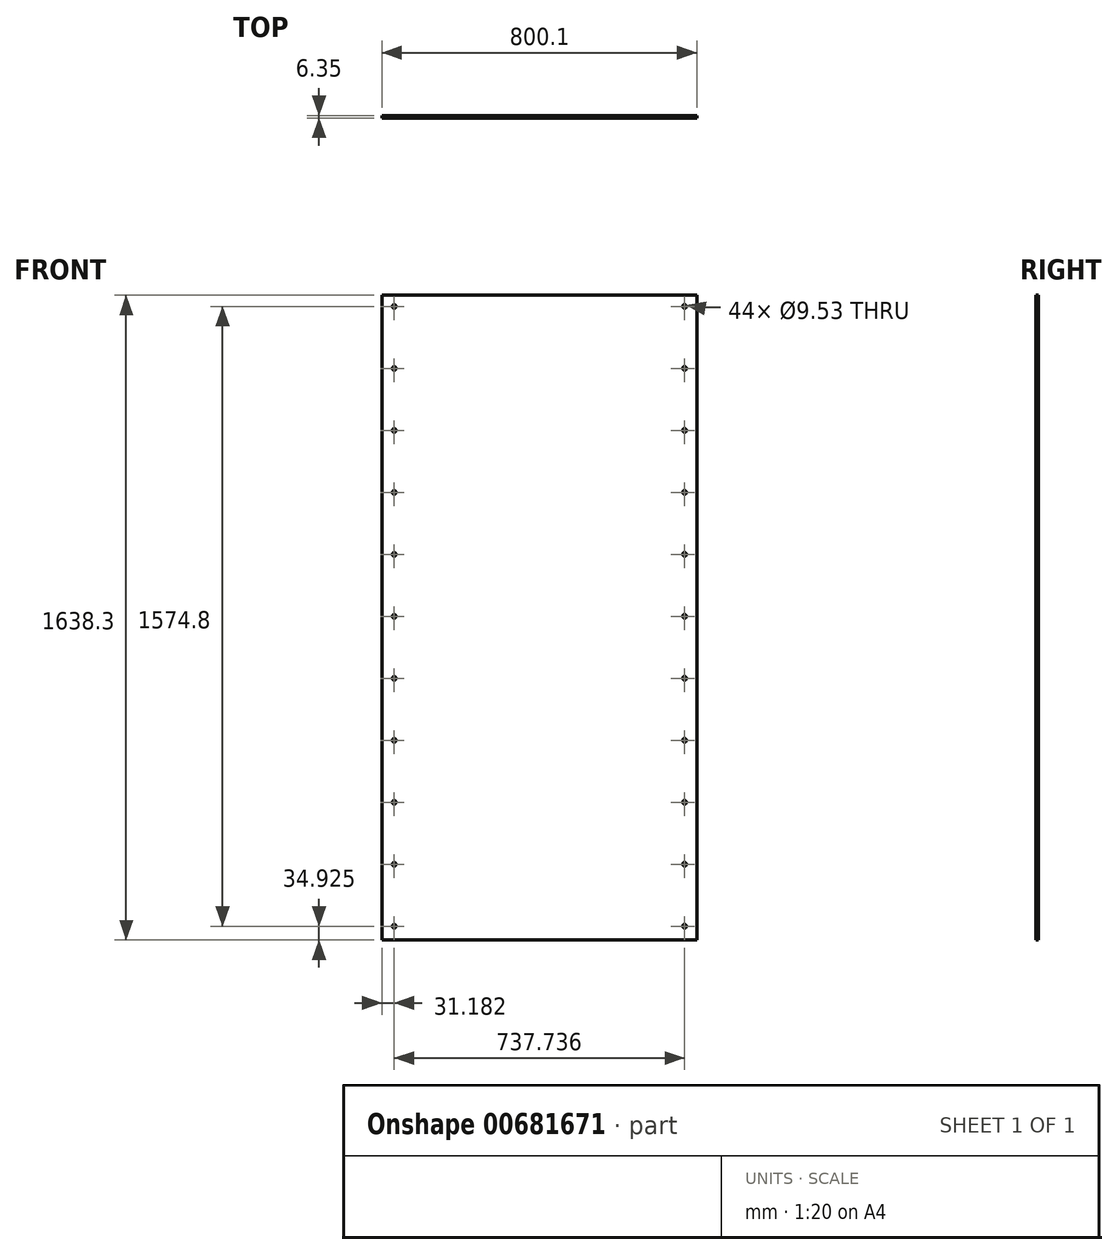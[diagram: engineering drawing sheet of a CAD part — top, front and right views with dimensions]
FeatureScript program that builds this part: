
annotation { "Feature Type Name" : "Feature", "Feature Type Description" : "" }
export const myFeature = defineFeature(function(context is Context, id is Id, definition is map)
    precondition{}
    {
        {
            var Q0;
            Q0=qCreatedBy(makeId("Front.planeOp"),FACE);
            var sketch = newSketch(context, id + "F0", { "sketchPlane" : qUnion([Q0])});
            skLineSegment(sketch, "E0.bottom", {"start": v(-400.05, 819.15) * mm, "end": v(400.05, 819.15) * mm});
            skLineSegment(sketch, "E0.top", {"start": v(-400.05, -819.15) * mm, "end": v(400.05, -819.15) * mm});
            skLineSegment(sketch, "E0.left", {"start": v(-400.05, 819.15) * mm, "end": v(-400.05, -819.15) * mm});
            skLineSegment(sketch, "E0.right", {"start": v(400.05, 819.15) * mm, "end": v(400.05, -819.15) * mm});
            skPoint(sketch, "E0.middle", {"position": v(0, 0) * mm});
            skLineSegment(sketch, "E1", {"start": v(-368.87, 819.15) * mm, "end": v(-368.87, -819.15) * mm, "construction": true});
            skLineSegment(sketch, "E2.bottom", {"start": v(-336.55, 762) * mm, "end": v(336.55, 762) * mm, "construction": true});
            skLineSegment(sketch, "E2.top", {"start": v(-336.55, -762) * mm, "end": v(336.55, -762) * mm, "construction": true});
            skLineSegment(sketch, "E2.left", {"start": v(-336.55, 762) * mm, "end": v(-336.55, -762) * mm, "construction": true});
            skLineSegment(sketch, "E2.right", {"start": v(336.55, 762) * mm, "end": v(336.55, -762) * mm, "construction": true});
            skLineSegment(sketch, "E3", {"start": v(0, 0) * mm, "end": v(-400.05, 0) * mm, "construction": true});
            skLineSegment(sketch, "E4", {"start": v(0, 0) * mm, "end": v(400.05, 0) * mm, "construction": true});
            skLineSegment(sketch, "E5", {"start": v(-431.98, 790.58) * mm, "end": v(468.8, 790.58) * mm, "construction": true});
            skLineSegment(sketch, "E6.MirrorCS", {"start": v(368.87, 819.15) * mm, "end": v(368.87, -819.15) * mm, "construction": true});
            skLineSegment(sketch, "E7.MirrorCS", {"start": v(-431.98, -790.58) * mm, "end": v(468.8, -790.57) * mm, "construction": true});
            skCircle(sketch, "E8", {"center": v(-368.87, 790.58) * mm, "radius": 4.76 * mm});
            skCircle(sketch, "E9.0.1.0", {"center": v(-368.87, 633.1) * mm, "radius": 4.76 * mm});
            skCircle(sketch, "E9.0.2.0", {"center": v(-368.87, 475.62) * mm, "radius": 4.76 * mm});
            skCircle(sketch, "E9.0.3.0", {"center": v(-368.87, 318.14) * mm, "radius": 4.76 * mm});
            skCircle(sketch, "E9.0.4.0", {"center": v(-368.87, 160.66) * mm, "radius": 4.76 * mm});
            skCircle(sketch, "E9.0.5.0", {"center": v(-368.87, 3.18) * mm, "radius": 4.76 * mm});
            skCircle(sketch, "E9.0.6.0", {"center": v(-368.87, -154.3) * mm, "radius": 4.76 * mm});
            skCircle(sketch, "E9.0.7.0", {"center": v(-368.87, -311.78) * mm, "radius": 4.76 * mm});
            skCircle(sketch, "E9.0.8.0", {"center": v(-368.87, -469.26) * mm, "radius": 4.76 * mm});
            skCircle(sketch, "E9.0.9.0", {"center": v(-368.87, -626.74) * mm, "radius": 4.76 * mm});
            skCircle(sketch, "E9.0.10.0", {"center": v(-368.87, -784.22) * mm, "radius": 4.76 * mm});
            skLineSegment(sketch, "E9.direction1", {"start": v(-368.87, 790.58) * mm, "end": v(-368.87, 790.58) * mm});
            skLineSegment(sketch, "E9.direction2", {"start": v(-368.87, 790.58) * mm, "end": v(-368.87, 633.1) * mm, "construction": true});
            skCircle(sketch, "E10.MirrorC", {"center": v(368.87, -784.22) * mm, "radius": 4.76 * mm});
            skCircle(sketch, "E11.MirrorC", {"center": v(368.87, -626.74) * mm, "radius": 4.76 * mm});
            skCircle(sketch, "E12.MirrorC", {"center": v(368.87, -469.26) * mm, "radius": 4.76 * mm});
            skCircle(sketch, "E13.MirrorC", {"center": v(368.87, -311.78) * mm, "radius": 4.76 * mm});
            skCircle(sketch, "E14.MirrorC", {"center": v(368.87, 3.18) * mm, "radius": 4.76 * mm});
            skCircle(sketch, "E15.MirrorC", {"center": v(368.87, 160.66) * mm, "radius": 4.76 * mm});
            skCircle(sketch, "E16.MirrorC", {"center": v(368.87, 318.14) * mm, "radius": 4.76 * mm});
            skCircle(sketch, "E17.MirrorC", {"center": v(368.87, 475.62) * mm, "radius": 4.76 * mm});
            skCircle(sketch, "E18.MirrorC", {"center": v(368.87, 633.1) * mm, "radius": 4.76 * mm});
            skCircle(sketch, "E19.MirrorC", {"center": v(368.87, 790.58) * mm, "radius": 4.76 * mm});
            skCircle(sketch, "E20.MirrorC", {"center": v(368.87, -154.3) * mm, "radius": 4.76 * mm});
            skLineSegment(sketch, "E21.MirrorCS", {"start": v(368.87, 790.58) * mm, "end": v(368.87, 633.1) * mm, "construction": true});
            skLineSegment(sketch, "E22.MirrorCS", {"start": v(368.87, 790.58) * mm, "end": v(368.87, 790.58) * mm});
            skSolve(sketch);
        }
        {
            var Q0;
            Q0=makeQuery(id+"F0.imprint","IMPRINT",FACE,{"disambiguationData":[TD([[makeQuery(id+"F0.imprint","IMPRINT",EDGE,{"derivedFrom":sQuery(id+"F0.wireOp",EDGE,"E0.bottom")}),-1.0]])]});
            extrude(context, id + "F1", {"entities" : qUnion([Q0]), "depth" : 6.35 * mm, "offsetDistance" : 25.4 * mm});
        }
        {
            var Q0;
            Q0=makeQuery(id+"F0.imprint","IMPRINT",FACE,{"disambiguationData":[TD([[makeQuery(id+"F0.imprint","IMPRINT",EDGE,{"derivedFrom":sQuery(id+"F0.wireOp",EDGE,"E0.bottom")}),-1.0]])]});
            extrude(context, id + "F2", {"entities" : qUnion([Q0]), "depth" : 5.08 * mm, "offsetDistance" : 25.4 * mm});
        }
    });
